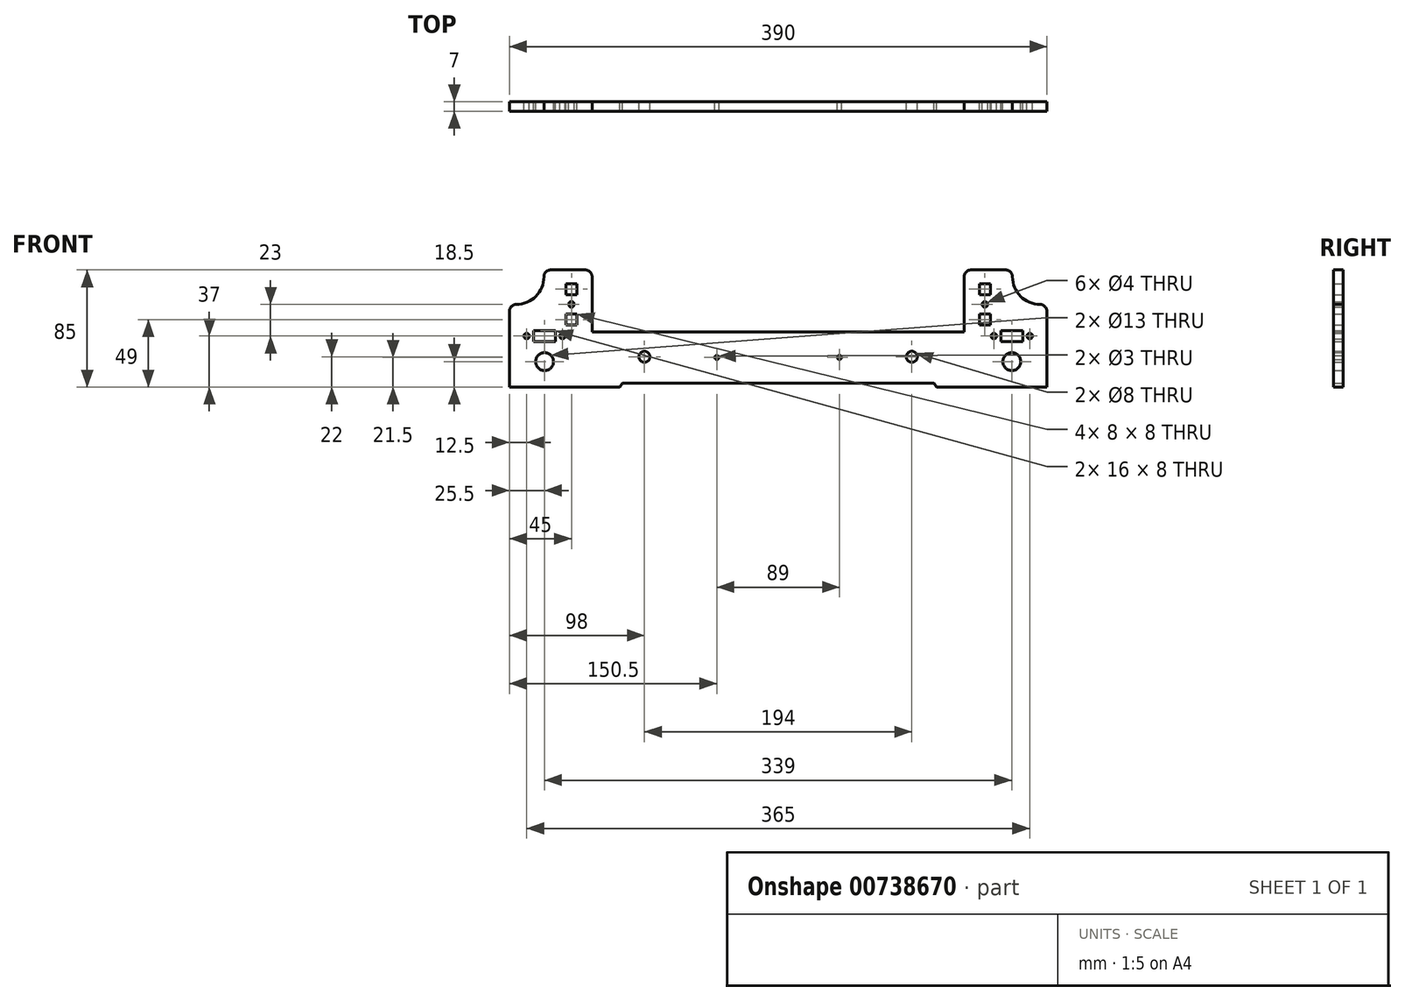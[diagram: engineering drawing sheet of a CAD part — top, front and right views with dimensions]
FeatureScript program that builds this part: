
annotation { "Feature Type Name" : "Feature", "Feature Type Description" : "" }
export const myFeature = defineFeature(function(context is Context, id is Id, definition is map)
    precondition{}
    {
        {
            var Q0;
            Q0=qCreatedBy(makeId("Front.planeOp"),FACE);
            var sketch = newSketch(context, id + "F0", { "sketchPlane" : qUnion([Q0])});
            skLineSegment(sketch, "E0", {"start": v(0, 0) * mm, "end": v(113, 0) * mm});
            skLineSegment(sketch, "E1", {"start": v(113, 0) * mm, "end": v(115, -3) * mm});
            skLineSegment(sketch, "E2", {"start": v(115, -3) * mm, "end": v(195, -3) * mm});
            skLineSegment(sketch, "E3", {"start": v(195, -3) * mm, "end": v(195, 52) * mm});
            skLineSegment(sketch, "E4", {"start": v(190, 57) * mm, "end": v(190, 57) * mm});
            skLineSegment(sketch, "E5", {"start": v(170, 77) * mm, "end": v(170, 77) * mm});
            skLineSegment(sketch, "E6", {"start": v(165, 82) * mm, "end": v(140, 82) * mm});
            skLineSegment(sketch, "E7", {"start": v(135, 77) * mm, "end": v(135, 46.75) * mm});
            skLineSegment(sketch, "E8", {"start": v(135, 46.75) * mm, "end": v(135, 37) * mm});
            skLineSegment(sketch, "E9", {"start": v(135, 37) * mm, "end": v(0, 37) * mm});
            skLineSegment(sketch, "E10", {"start": v(0, 37) * mm, "end": v(0, 0) * mm, "construction": true});
            skPoint(sketch, "E11.visualSharp", {"position": v(170, 57) * mm});
            skArc(sketch, "E11.filletArc", {"start": v(170, 77) * mm, "mid": v(175.86, 62.86) * mm, "end": v(190, 57) * mm});
            skPoint(sketch, "E12.visualSharp", {"position": v(135, 82) * mm});
            skArc(sketch, "E12.filletArc", {"start": v(140, 82) * mm, "mid": v(136.46, 80.54) * mm, "end": v(135, 77) * mm});
            skPoint(sketch, "E13.visualSharp", {"position": v(170, 82) * mm});
            skArc(sketch, "E13.filletArc", {"start": v(170, 77) * mm, "mid": v(168.54, 80.54) * mm, "end": v(165, 82) * mm});
            skPoint(sketch, "E14.visualSharp", {"position": v(195, 57) * mm});
            skArc(sketch, "E14.filletArc", {"start": v(195, 52) * mm, "mid": v(193.54, 55.54) * mm, "end": v(190, 57) * mm});
            skCircle(sketch, "E15", {"center": v(169.5, 15.5) * mm, "radius": 6.5 * mm});
            skLineSegment(sketch, "E16", {"start": v(169.5, -3) * mm, "end": v(169.5, 46.8) * mm, "construction": true});
            skLineSegment(sketch, "E17.bottom", {"start": v(177.5, 38) * mm, "end": v(161.5, 38) * mm});
            skLineSegment(sketch, "E17.top", {"start": v(177.5, 30) * mm, "end": v(161.5, 30) * mm});
            skLineSegment(sketch, "E17.left", {"start": v(177.5, 38) * mm, "end": v(177.5, 30) * mm});
            skLineSegment(sketch, "E17.right", {"start": v(161.5, 38) * mm, "end": v(161.5, 30) * mm});
            skPoint(sketch, "E17.middle", {"position": v(169.5, 34) * mm});
            skCircle(sketch, "E18", {"center": v(182.5, 34) * mm, "radius": 2 * mm});
            skPoint(sketch, "E18.centerSnap0", {"position": v(177.5, 34) * mm});
            skCircle(sketch, "E19.MirrorC", {"center": v(156.5, 34) * mm, "radius": 2 * mm});
            skCircle(sketch, "E20", {"center": v(150, 57) * mm, "radius": 2 * mm});
            skLineSegment(sketch, "E21", {"start": v(148, 57) * mm, "end": v(152, 57) * mm, "construction": true});
            skLineSegment(sketch, "E22.bottom", {"start": v(154, 72) * mm, "end": v(146, 72) * mm});
            skLineSegment(sketch, "E22.top", {"start": v(154, 64) * mm, "end": v(146, 64) * mm});
            skLineSegment(sketch, "E22.left", {"start": v(154, 72) * mm, "end": v(154, 64) * mm});
            skLineSegment(sketch, "E22.right", {"start": v(146, 72) * mm, "end": v(146, 64) * mm});
            skPoint(sketch, "E22.middle", {"position": v(150, 68) * mm});
            skLineSegment(sketch, "E23.MirrorCS", {"start": v(154, 42) * mm, "end": v(146, 42) * mm});
            skLineSegment(sketch, "E24.MirrorCS", {"start": v(146, 42) * mm, "end": v(146, 50) * mm});
            skLineSegment(sketch, "E25.MirrorCS", {"start": v(154, 50) * mm, "end": v(146, 50) * mm});
            skPoint(sketch, "E26.MirrorP", {"position": v(150, 46) * mm});
            skLineSegment(sketch, "E27.MirrorCS", {"start": v(154, 42) * mm, "end": v(154, 50) * mm});
            skCircle(sketch, "E28", {"center": v(44.5, 18.5) * mm, "radius": 1.5 * mm});
            skCircle(sketch, "E29", {"center": v(97, 19) * mm, "radius": 4 * mm});
            skLineSegment(sketch, "E30.MirrorCS", {"start": v(-148, 57) * mm, "end": v(-152, 57) * mm, "construction": true});
            skLineSegment(sketch, "E31.MirrorCS", {"start": v(-154, 72) * mm, "end": v(-154, 64) * mm});
            skLineSegment(sketch, "E32.MirrorCS", {"start": v(-154, 72) * mm, "end": v(-146, 72) * mm});
            skArc(sketch, "E33.MirrorCS", {"start": v(-195, 52) * mm, "mid": v(-193.54, 55.54) * mm, "end": v(-190, 57) * mm});
            skArc(sketch, "E34.MirrorCS", {"start": v(-170, 77) * mm, "mid": v(-168.54, 80.54) * mm, "end": v(-165, 82) * mm});
            skArc(sketch, "E35.MirrorCS", {"start": v(-140, 82) * mm, "mid": v(-136.46, 80.54) * mm, "end": v(-135, 77) * mm});
            skLineSegment(sketch, "E36.MirrorCS", {"start": v(-177.5, 38) * mm, "end": v(-177.5, 30) * mm});
            skCircle(sketch, "E37.MirrorC", {"center": v(-150, 57) * mm, "radius": 2 * mm});
            skLineSegment(sketch, "E38.MirrorCS", {"start": v(-146, 72) * mm, "end": v(-146, 64) * mm});
            skLineSegment(sketch, "E39.MirrorCS", {"start": v(-161.5, 38) * mm, "end": v(-161.5, 30) * mm});
            skCircle(sketch, "E40.MirrorC", {"center": v(-44.5, 18.5) * mm, "radius": 1.5 * mm});
            skLineSegment(sketch, "E41.MirrorCS", {"start": v(-177.5, 30) * mm, "end": v(-161.5, 30) * mm});
            skLineSegment(sketch, "E42.MirrorCS", {"start": v(-154, 50) * mm, "end": v(-146, 50) * mm});
            skLineSegment(sketch, "E43.MirrorCS", {"start": v(-154, 42) * mm, "end": v(-146, 42) * mm});
            skLineSegment(sketch, "E44.MirrorCS", {"start": v(-135, 46.75) * mm, "end": v(-135, 37) * mm});
            skLineSegment(sketch, "E45.MirrorCS", {"start": v(-113, 0) * mm, "end": v(-115, -3) * mm});
            skLineSegment(sketch, "E46.MirrorCS", {"start": v(-177.5, 38) * mm, "end": v(-161.5, 38) * mm});
            skLineSegment(sketch, "E47.MirrorCS", {"start": v(-154, 42) * mm, "end": v(-154, 50) * mm});
            skLineSegment(sketch, "E48.MirrorCS", {"start": v(-154, 64) * mm, "end": v(-146, 64) * mm});
            skLineSegment(sketch, "E49.MirrorCS", {"start": v(-146, 42) * mm, "end": v(-146, 50) * mm});
            skCircle(sketch, "E50.MirrorC", {"center": v(-182.5, 34) * mm, "radius": 2 * mm});
            skCircle(sketch, "E51.MirrorC", {"center": v(-97, 19) * mm, "radius": 4 * mm});
            skCircle(sketch, "E52.MirrorC", {"center": v(-156.5, 34) * mm, "radius": 2 * mm});
            skLineSegment(sketch, "E53.MirrorCS", {"start": v(-165, 82) * mm, "end": v(-140, 82) * mm});
            skPoint(sketch, "E54.MirrorP", {"position": v(-150, 68) * mm});
            skLineSegment(sketch, "E55.MirrorCS", {"start": v(-169.5, -3) * mm, "end": v(-169.5, 46.8) * mm, "construction": true});
            skPoint(sketch, "E56.MirrorP", {"position": v(-177.5, 34) * mm});
            skLineSegment(sketch, "E57.MirrorCS", {"start": v(-170, 77) * mm, "end": v(-170, 77) * mm});
            skArc(sketch, "E58.MirrorCS", {"start": v(-170, 77) * mm, "mid": v(-175.86, 62.86) * mm, "end": v(-190, 57) * mm});
            skLineSegment(sketch, "E59.MirrorCS", {"start": v(-135, 37) * mm, "end": v(0, 37) * mm});
            skLineSegment(sketch, "E60.MirrorCS", {"start": v(-135, 77) * mm, "end": v(-135, 46.75) * mm});
            skLineSegment(sketch, "E61.MirrorCS", {"start": v(-195, -3) * mm, "end": v(-195, 52) * mm});
            skLineSegment(sketch, "E62.MirrorCS", {"start": v(-115, -3) * mm, "end": v(-195, -3) * mm});
            skPoint(sketch, "E63.MirrorP", {"position": v(-170, 57) * mm});
            skPoint(sketch, "E64.MirrorP", {"position": v(-135, 82) * mm});
            skPoint(sketch, "E65.MirrorP", {"position": v(-169.5, 34) * mm});
            skLineSegment(sketch, "E66.MirrorCS", {"start": v(-190, 57) * mm, "end": v(-190, 57) * mm});
            skLineSegment(sketch, "E67.MirrorCS", {"start": v(0, 0) * mm, "end": v(-113, 0) * mm});
            skCircle(sketch, "E68.MirrorC", {"center": v(-169.5, 15.5) * mm, "radius": 6.5 * mm});
            skPoint(sketch, "E69.MirrorP", {"position": v(-170, 82) * mm});
            skPoint(sketch, "E70.MirrorP", {"position": v(-195, 57) * mm});
            skPoint(sketch, "E71.MirrorP", {"position": v(-150, 46) * mm});
            skSolve(sketch);
        }
        {
            var Q0;
            Q0 = qSketchRegion(id + "F0", true);
            extrude(context, id + "F1", {"entities" : qUnion([Q0]), "depth" : 7 * mm, "offsetDistance" : 25 * mm});
        }
    });
